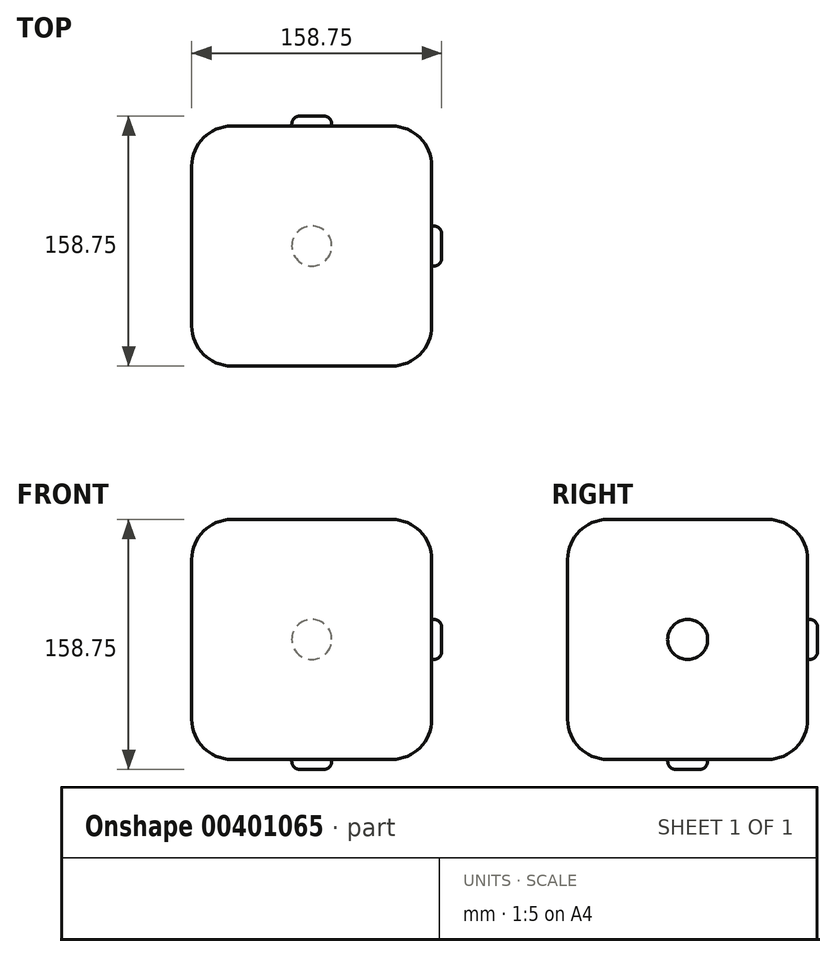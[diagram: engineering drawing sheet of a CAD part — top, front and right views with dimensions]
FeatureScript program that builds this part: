
annotation { "Feature Type Name" : "Feature", "Feature Type Description" : "" }
export const myFeature = defineFeature(function(context is Context, id is Id, definition is map)
    precondition{}
    {
        {
            var Q0;
            Q0=qCreatedBy(makeId("Top.planeOp"),FACE);
            var sketch = newSketch(context, id + "F0", { "sketchPlane" : qUnion([Q0])});
            skLineSegment(sketch, "E0.bottom", {"start": v(-76.2, 76.2) * mm, "end": v(76.2, 76.2) * mm});
            skLineSegment(sketch, "E0.top", {"start": v(-76.2, -76.2) * mm, "end": v(76.2, -76.2) * mm});
            skLineSegment(sketch, "E0.left", {"start": v(-76.2, 76.2) * mm, "end": v(-76.2, -76.2) * mm});
            skLineSegment(sketch, "E0.right", {"start": v(76.2, 76.2) * mm, "end": v(76.2, -76.2) * mm});
            skSolve(sketch);
        }
        {
            var Q0;
            Q0=makeQuery(id+"F0.imprint","IMPRINT",FACE,{"disambiguationData":[TD([[makeQuery(id+"F0.imprint","IMPRINT",EDGE,{"derivedFrom":sQuery(id+"F0.wireOp",EDGE,"E0.bottom")}),-1.0]])]});
            extrude(context, id + "F1", {"entities" : qUnion([Q0]), "depth" : 152.4 * mm});
        }
        {
            var Q0;
            Q0=makeQuery(id+"F1.opExtrude","CAP_FACE",FACE,{"disambiguationData":[OSD([sQuery(id+"F0.wireOp",EDGE,"E0.bottom"),sQuery(id+"F0.wireOp",EDGE,"E0.top"),sQuery(id+"F0.wireOp",EDGE,"E0.left"),sQuery(id+"F0.wireOp",EDGE,"E0.right")])],"isStart":false});
            var Q1;
            Q1=makeQuery(id+"F1.opExtrude","SWEPT_FACE",FACE,{"disambiguationData":[OSD([sQuery(id+"F0.wireOp",EDGE,"E0.top")])]});
            var Q2;
            Q2=makeQuery(id+"F1.opExtrude","SWEPT_FACE",FACE,{"disambiguationData":[OSD([sQuery(id+"F0.wireOp",EDGE,"E0.right")])]});
            var Q3;
            Q3=makeQuery(id+"F1.opExtrude","SWEPT_FACE",FACE,{"disambiguationData":[OSD([sQuery(id+"F0.wireOp",EDGE,"E0.left")])]});
            var Q4;
            Q4=makeQuery(id+"F1.opExtrude","SWEPT_FACE",FACE,{"disambiguationData":[OSD([sQuery(id+"F0.wireOp",EDGE,"E0.bottom")])]});
            var Q5;
            Q5=makeQuery(id+"F1.opExtrude","CAP_FACE",FACE,{"disambiguationData":[OSD([sQuery(id+"F0.wireOp",EDGE,"E0.bottom"),sQuery(id+"F0.wireOp",EDGE,"E0.top"),sQuery(id+"F0.wireOp",EDGE,"E0.left"),sQuery(id+"F0.wireOp",EDGE,"E0.right")])],"isStart":true});
            fillet(context, id + "F2", {"entities" : qUnion([Q0, Q1, Q2, Q3, Q4, Q5]), "radius" : 25.4 * mm, "tangentPropagation" : true, "allowEdgeOverflow" : false});
        }
        {
            var Q0;
            Q0=makeQuery(id+"F1.opExtrude","CAP_FACE",FACE,{"disambiguationData":[OSD([sQuery(id+"F0.wireOp",EDGE,"E0.bottom"),sQuery(id+"F0.wireOp",EDGE,"E0.top"),sQuery(id+"F0.wireOp",EDGE,"E0.left"),sQuery(id+"F0.wireOp",EDGE,"E0.right")])],"isStart":true});
            var sketch = newSketch(context, id + "F3", { "sketchPlane" : qUnion([Q0])});
            skCircle(sketch, "E1", {"center": v(0, 0) * mm, "radius": 12.7 * mm});
            skSolve(sketch);
        }
        {
            var Q0;
            Q0=makeQuery(id+"F3.imprint","IMPRINT",FACE,{"disambiguationData":[TD([[makeQuery(id+"F3.imprint","IMPRINT",EDGE,{"derivedFrom":sQuery(id+"F3.wireOp",EDGE,"E1")}),1.0]])]});
            extrude(context, id + "F4", {"entities" : qUnion([Q0]), "operationType" : NewBodyOperationType.ADD, "depth" : 6.35 * mm});
        }
        {
            var Q0;
            Q0=makeQuery(id+"F4.opExtrude","CAP_EDGE",EDGE,{"disambiguationData":[OSD([sQuery(id+"F3.wireOp",EDGE,"E1")])],"isStart":false});
            fillet(context, id + "F5", {"entities" : qUnion([Q0]), "radius" : 5.08 * mm, "tangentPropagation" : true, "allowEdgeOverflow" : false});
        }
        {
            var Q0;
            Q0=makeQuery(id+"F1.opExtrude","SWEPT_FACE",FACE,{"disambiguationData":[OSD([sQuery(id+"F0.wireOp",EDGE,"E0.bottom")])]});
            var sketch = newSketch(context, id + "F6", { "sketchPlane" : qUnion([Q0])});
            skCircle(sketch, "E2", {"center": v(0, 76.2) * mm, "radius": 12.7 * mm});
            skPoint(sketch, "E2.centerSnap0", {"position": v(-50.8, 76.2) * mm});
            skPoint(sketch, "E2.centerSnap1", {"position": v(0, 127) * mm});
            skSolve(sketch);
        }
        {
            var Q0;
            Q0=makeQuery(id+"F6.imprint","IMPRINT",FACE,{"disambiguationData":[TD([[makeQuery(id+"F6.imprint","IMPRINT",EDGE,{"derivedFrom":sQuery(id+"F6.wireOp",EDGE,"E2")}),1.0]])]});
            extrude(context, id + "F7", {"entities" : qUnion([Q0]), "operationType" : NewBodyOperationType.ADD, "depth" : 6.35 * mm});
        }
        {
            var Q0;
            Q0=makeQuery(id+"F7.opExtrude","CAP_EDGE",EDGE,{"disambiguationData":[OSD([sQuery(id+"F6.wireOp",EDGE,"E2")])],"isStart":false});
            fillet(context, id + "F8", {"entities" : qUnion([Q0]), "radius" : 5.08 * mm, "tangentPropagation" : true, "allowEdgeOverflow" : false});
        }
        {
            var Q0;
            Q0=makeQuery(id+"F1.opExtrude","SWEPT_FACE",FACE,{"disambiguationData":[OSD([sQuery(id+"F0.wireOp",EDGE,"E0.right")])]});
            var sketch = newSketch(context, id + "F9", { "sketchPlane" : qUnion([Q0])});
            skCircle(sketch, "E3", {"center": v(0, 76.2) * mm, "radius": 12.7 * mm});
            skPoint(sketch, "E3.centerSnap0", {"position": v(50.8, 76.2) * mm});
            skSolve(sketch);
        }
        {
            var Q0;
            Q0=makeQuery(id+"F9.imprint","IMPRINT",FACE,{"disambiguationData":[TD([[makeQuery(id+"F9.imprint","IMPRINT",EDGE,{"derivedFrom":sQuery(id+"F9.wireOp",EDGE,"E3")}),1.0]])]});
            extrude(context, id + "F10", {"entities" : qUnion([Q0]), "depth" : 6.35 * mm});
        }
        {
            var Q0;
            Q0=makeQuery(id+"F10.opExtrude","CAP_EDGE",EDGE,{"disambiguationData":[OSD([sQuery(id+"F9.wireOp",EDGE,"E3")])],"isStart":false});
            fillet(context, id + "F11", {"entities" : qUnion([Q0]), "radius" : 5.08 * mm, "tangentPropagation" : true, "allowEdgeOverflow" : false});
        }
    });
